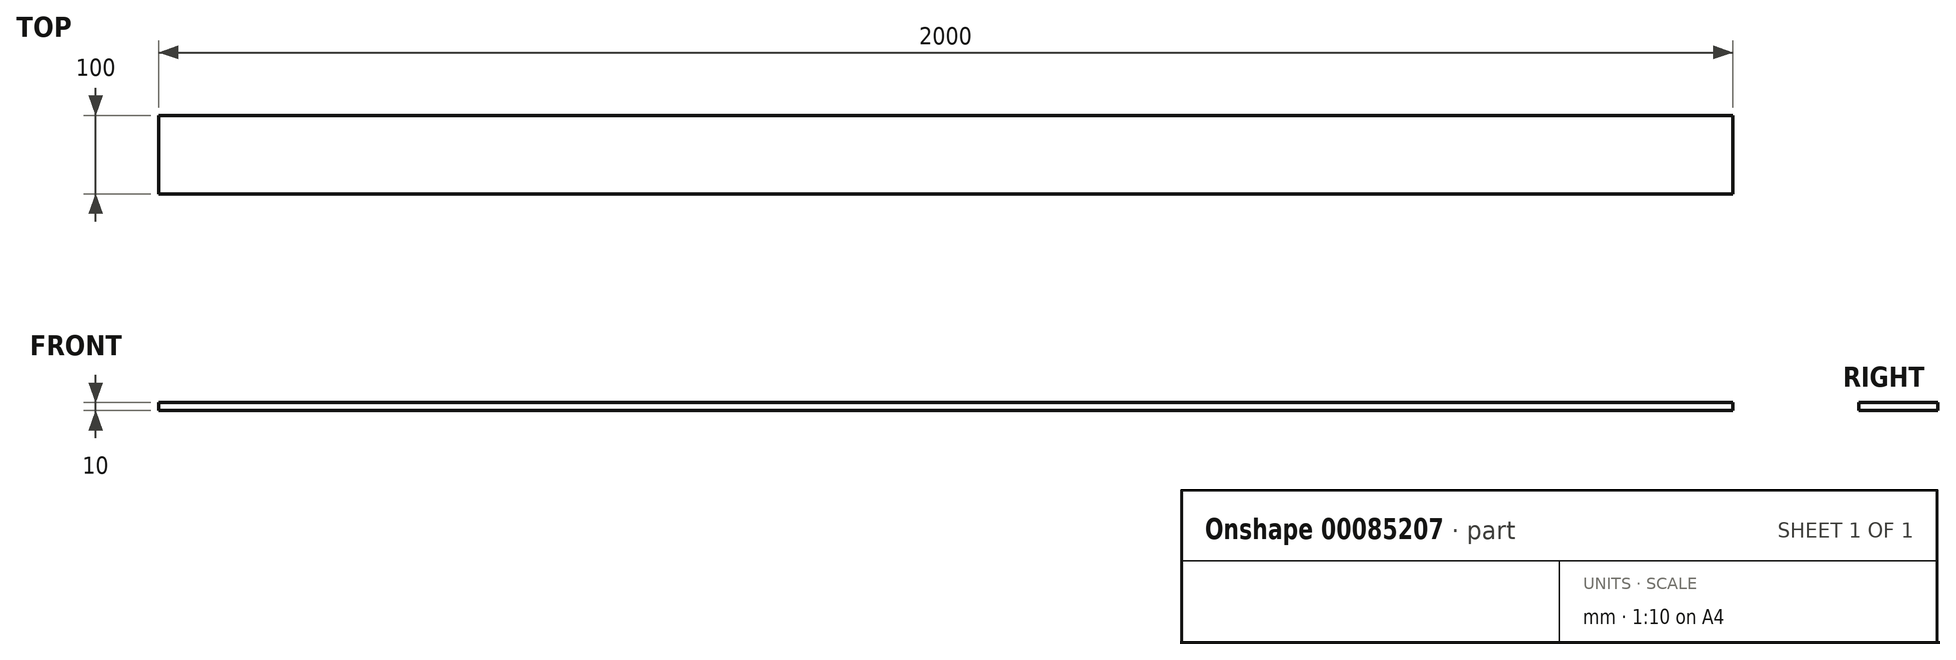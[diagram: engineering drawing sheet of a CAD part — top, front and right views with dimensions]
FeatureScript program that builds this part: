
annotation { "Feature Type Name" : "Feature", "Feature Type Description" : "" }
export const myFeature = defineFeature(function(context is Context, id is Id, definition is map)
    precondition{}
    {
        {
            var Q0;
            Q0=qCreatedBy(makeId("Right.planeOp"),FACE);
            var sketch = newSketch(context, id + "F0", { "sketchPlane" : qUnion([Q0])});
            skLineSegment(sketch, "E0.bottom", {"start": v(-50, 5) * mm, "end": v(50, 5) * mm});
            skLineSegment(sketch, "E0.top", {"start": v(-50, -5) * mm, "end": v(50, -5) * mm});
            skLineSegment(sketch, "E0.left", {"start": v(-50, 5) * mm, "end": v(-50, -5) * mm});
            skLineSegment(sketch, "E0.right", {"start": v(50, 5) * mm, "end": v(50, -5) * mm});
            skSolve(sketch);
        }
        {
            var Q0;
            Q0=makeQuery(id+"F0.imprint","IMPRINT",FACE,{"disambiguationData":[TD([[makeQuery(id+"F0.imprint","IMPRINT",EDGE,{"derivedFrom":sQuery(id+"F0.wireOp",EDGE,"E0.bottom")}),-1.0]])]});
            extrude(context, id + "F1", {"entities" : qUnion([Q0]), "depth" : 2000 * mm});
        }
    });
